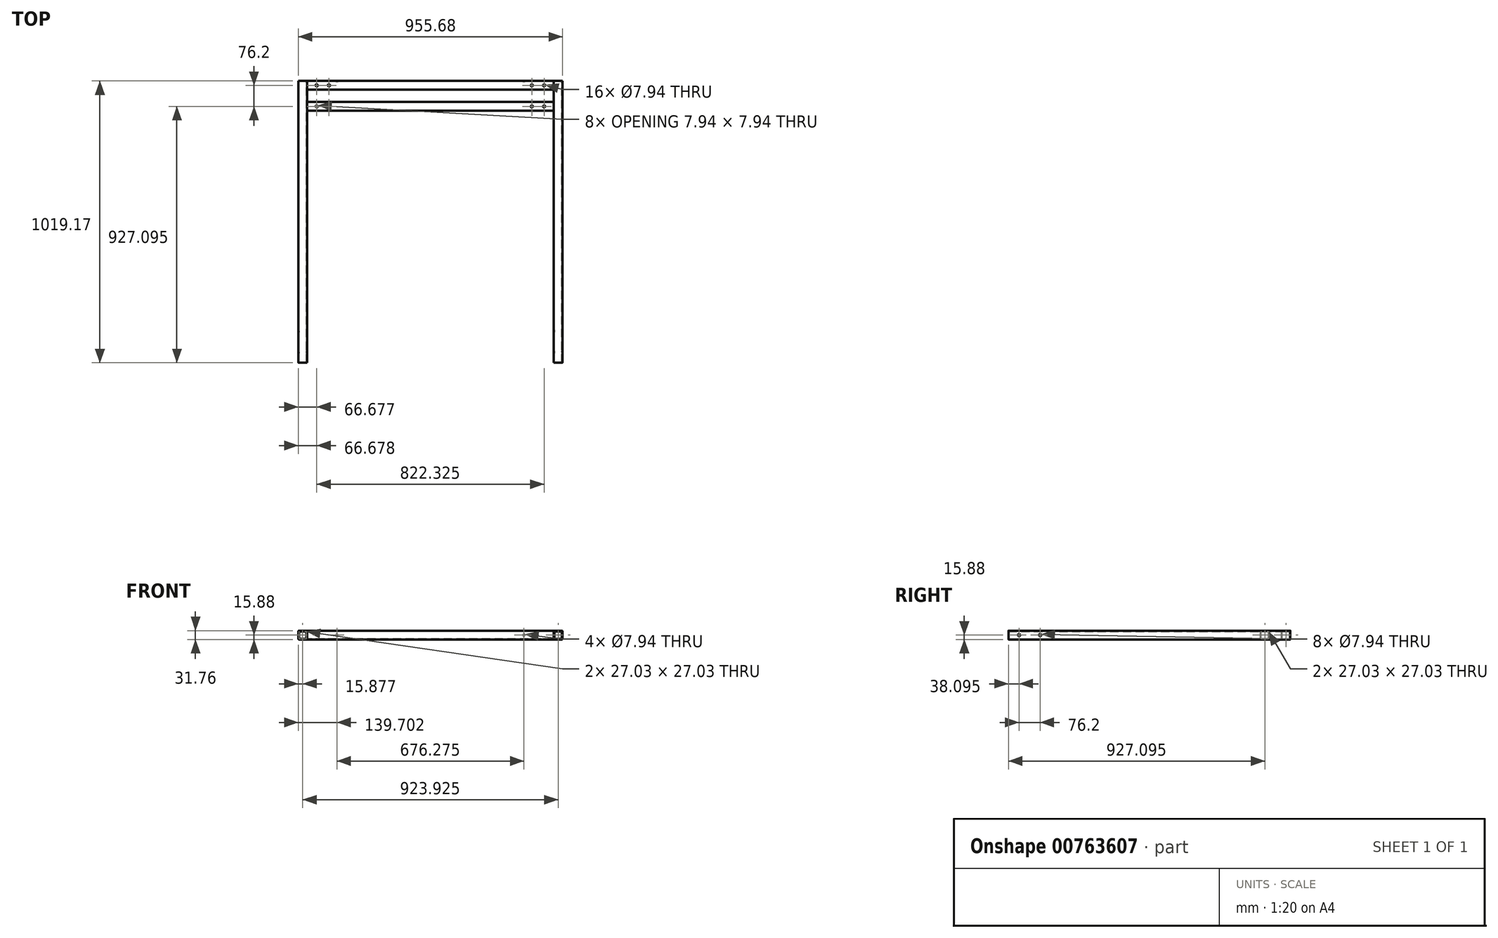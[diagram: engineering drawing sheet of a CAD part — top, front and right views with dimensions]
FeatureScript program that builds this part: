
annotation { "Feature Type Name" : "Feature", "Feature Type Description" : "" }
export const myFeature = defineFeature(function(context is Context, id is Id, definition is map)
    precondition{}
    {
        {
            var Q0;
            Q0=qCreatedBy(makeId("Front.planeOp"),FACE);
            var sketch = newSketch(context, id + "F0", { "sketchPlane" : qUnion([Q0])});
            skLineSegment(sketch, "E0.bottom", {"start": v(-448.45, -15.87) * mm, "end": v(-475.48, -15.87) * mm});
            skLineSegment(sketch, "E0.top", {"start": v(-448.45, 15.88) * mm, "end": v(-475.48, 15.88) * mm});
            skLineSegment(sketch, "E0.left", {"start": v(-446.09, -13.51) * mm, "end": v(-446.09, 13.51) * mm});
            skLineSegment(sketch, "E0.right", {"start": v(-477.84, -13.51) * mm, "end": v(-477.84, 13.51) * mm});
            skPoint(sketch, "E0.middle", {"position": v(-461.96, 0) * mm});
            skPoint(sketch, "E1.visualSharp", {"position": v(-446.09, 15.88) * mm});
            skArc(sketch, "E1.filletArc", {"start": v(-446.09, 13.51) * mm, "mid": v(-446.78, 15.18) * mm, "end": v(-448.45, 15.88) * mm});
            skPoint(sketch, "E2.visualSharp", {"position": v(-446.09, -15.87) * mm});
            skArc(sketch, "E2.filletArc", {"start": v(-448.45, -15.87) * mm, "mid": v(-446.78, -15.18) * mm, "end": v(-446.09, -13.51) * mm});
            skPoint(sketch, "E3.visualSharp", {"position": v(-477.84, -15.87) * mm});
            skArc(sketch, "E3.filletArc", {"start": v(-477.84, -13.51) * mm, "mid": v(-477.15, -15.18) * mm, "end": v(-475.48, -15.87) * mm});
            skPoint(sketch, "E4.visualSharp", {"position": v(-477.84, 15.88) * mm});
            skArc(sketch, "E4.filletArc", {"start": v(-475.48, 15.88) * mm, "mid": v(-477.15, 15.18) * mm, "end": v(-477.84, 13.51) * mm});
            skLineSegment(sketch, "E5.0", {"start": v(-448.45, 13.51) * mm, "end": v(-475.48, 13.51) * mm});
            skLineSegment(sketch, "E5.1", {"start": v(-448.45, -13.51) * mm, "end": v(-448.45, 13.51) * mm});
            skLineSegment(sketch, "E5.2", {"start": v(-448.45, -13.51) * mm, "end": v(-475.48, -13.51) * mm});
            skLineSegment(sketch, "E5.3", {"start": v(-475.48, -13.51) * mm, "end": v(-475.48, 13.51) * mm});
            skLineSegment(sketch, "E6", {"start": v(-461.96, 0) * mm, "end": v(0, 0) * mm, "construction": true});
            skSolve(sketch);
        }
        {
            var Q0;
            Q0=makeQuery(id+"F0.imprint","IMPRINT",FACE,{"disambiguationData":[TD([[makeQuery(id+"F0.imprint","IMPRINT",EDGE,{"derivedFrom":sQuery(id+"F0.wireOp",EDGE,"E0.bottom")}),-1.0]])]});
            extrude(context, id + "F1", {"entities" : qUnion([Q0]), "depth" : 1019.17 * mm, "offsetDistance" : 25.4 * mm});
        }
        {
            var Q0;
            Q0=makeQuery(id+"F1.opExtrude","SWEPT_FACE",FACE,{"disambiguationData":[OSD([sQuery(id+"F0.wireOp",EDGE,"E0.left")])]});
            var sketch = newSketch(context, id + "F2", { "sketchPlane" : qUnion([Q0])});
            skLineSegment(sketch, "E7.bottom", {"start": v(-2.36, -15.88) * mm, "end": v(-29.39, -15.88) * mm});
            skLineSegment(sketch, "E7.top", {"start": v(-2.36, 15.87) * mm, "end": v(-29.39, 15.87) * mm});
            skLineSegment(sketch, "E7.left", {"start": v(0, -13.51) * mm, "end": v(0, 13.51) * mm});
            skLineSegment(sketch, "E7.right", {"start": v(-31.75, -13.51) * mm, "end": v(-31.75, 13.51) * mm});
            skPoint(sketch, "E7.middle", {"position": v(-15.88, 0) * mm});
            skPoint(sketch, "E8.visualSharp", {"position": v(0, 15.87) * mm});
            skArc(sketch, "E8.filletArc", {"start": v(0, 13.51) * mm, "mid": v(-0.7, 15.18) * mm, "end": v(-2.36, 15.87) * mm});
            skPoint(sketch, "E9.visualSharp", {"position": v(0, -15.88) * mm});
            skArc(sketch, "E9.filletArc", {"start": v(-2.36, -15.88) * mm, "mid": v(-0.7, -15.18) * mm, "end": v(0, -13.51) * mm});
            skPoint(sketch, "E10.visualSharp", {"position": v(-31.75, -15.88) * mm});
            skArc(sketch, "E10.filletArc", {"start": v(-31.75, -13.51) * mm, "mid": v(-31.06, -15.18) * mm, "end": v(-29.39, -15.88) * mm});
            skPoint(sketch, "E11.visualSharp", {"position": v(-31.75, 15.87) * mm});
            skArc(sketch, "E11.filletArc", {"start": v(-29.39, 15.87) * mm, "mid": v(-31.06, 15.18) * mm, "end": v(-31.75, 13.51) * mm});
            skLineSegment(sketch, "E12.0", {"start": v(-2.36, 13.51) * mm, "end": v(-29.39, 13.51) * mm});
            skLineSegment(sketch, "E12.1", {"start": v(-2.36, -13.51) * mm, "end": v(-2.36, 13.51) * mm});
            skLineSegment(sketch, "E12.2", {"start": v(-2.36, -13.51) * mm, "end": v(-29.39, -13.51) * mm});
            skLineSegment(sketch, "E12.3", {"start": v(-29.39, -13.51) * mm, "end": v(-29.39, 13.51) * mm});
            skLineSegment(sketch, "E13.bottom", {"start": v(-78.56, -15.88) * mm, "end": v(-105.59, -15.88) * mm});
            skLineSegment(sketch, "E13.top", {"start": v(-78.56, 15.87) * mm, "end": v(-105.59, 15.87) * mm});
            skLineSegment(sketch, "E13.left", {"start": v(-76.2, -13.51) * mm, "end": v(-76.2, 13.51) * mm});
            skLineSegment(sketch, "E13.right", {"start": v(-107.95, -13.51) * mm, "end": v(-107.95, 13.51) * mm});
            skPoint(sketch, "E13.middle", {"position": v(-92.08, 0) * mm});
            skPoint(sketch, "E14.visualSharp", {"position": v(-76.2, 15.87) * mm});
            skArc(sketch, "E14.filletArc", {"start": v(-76.2, 13.51) * mm, "mid": v(-76.9, 15.18) * mm, "end": v(-78.56, 15.87) * mm});
            skPoint(sketch, "E15.visualSharp", {"position": v(-76.2, -15.88) * mm});
            skArc(sketch, "E15.filletArc", {"start": v(-78.56, -15.88) * mm, "mid": v(-76.9, -15.18) * mm, "end": v(-76.2, -13.51) * mm});
            skPoint(sketch, "E16.visualSharp", {"position": v(-107.95, -15.88) * mm});
            skArc(sketch, "E16.filletArc", {"start": v(-107.95, -13.51) * mm, "mid": v(-107.26, -15.18) * mm, "end": v(-105.59, -15.88) * mm});
            skPoint(sketch, "E17.visualSharp", {"position": v(-107.95, 15.87) * mm});
            skArc(sketch, "E17.filletArc", {"start": v(-105.59, 15.87) * mm, "mid": v(-107.26, 15.18) * mm, "end": v(-107.95, 13.51) * mm});
            skLineSegment(sketch, "E18.0", {"start": v(-78.56, 13.51) * mm, "end": v(-105.59, 13.51) * mm});
            skLineSegment(sketch, "E18.1", {"start": v(-78.56, -13.51) * mm, "end": v(-78.56, 13.51) * mm});
            skLineSegment(sketch, "E18.2", {"start": v(-78.56, -13.51) * mm, "end": v(-105.59, -13.51) * mm});
            skLineSegment(sketch, "E18.3", {"start": v(-105.59, -13.51) * mm, "end": v(-105.59, 13.51) * mm});
            skSolve(sketch);
        }
        {
            var Q0;
            {var subQ0=sQuery(id+"F2.wireOp",EDGE,"E13.right");Q0=makeQuery(id+"F2.imprint","IMPRINT",FACE,{"disambiguationData":[TD([[makeQuery(id+"F2.imprint","IMPRINT",EDGE,{"derivedFrom":subQ0}),-1.0]])]});}
            var Q1;
            Q1=makeQuery(id+"F2.imprint","IMPRINT",FACE,{"disambiguationData":[TD([[makeQuery(id+"F2.imprint","IMPRINT",EDGE,{"derivedFrom":sQuery(id+"F2.wireOp",EDGE,"E13.top")}),1.0]])]});
            var Q2;
            {var subQ0=sQuery(id+"F2.wireOp",EDGE,"E13.left");Q2=makeQuery(id+"F2.imprint","IMPRINT",FACE,{"disambiguationData":[TD([[makeQuery(id+"F2.imprint","IMPRINT",EDGE,{"derivedFrom":subQ0}),1.0]])]});}
            var Q3;
            Q3=makeQuery(id+"F2.imprint","IMPRINT",FACE,{"disambiguationData":[TD([[makeQuery(id+"F2.imprint","IMPRINT",EDGE,{"derivedFrom":sQuery(id+"F2.wireOp",EDGE,"E13.bottom")}),-1.0]])]});
            var Q4;
            {var subQ0=sQuery(id+"F2.wireOp",EDGE,"E7.right");Q4=makeQuery(id+"F2.imprint","IMPRINT",FACE,{"disambiguationData":[TD([[makeQuery(id+"F2.imprint","IMPRINT",EDGE,{"derivedFrom":subQ0}),-1.0]])]});}
            var Q5;
            Q5=makeQuery(id+"F2.imprint","IMPRINT",FACE,{"disambiguationData":[TD([[makeQuery(id+"F2.imprint","IMPRINT",EDGE,{"derivedFrom":sQuery(id+"F2.wireOp",EDGE,"E7.top")}),1.0]])]});
            var Q6;
            {var subQ0=sQuery(id+"F2.wireOp",EDGE,"E7.left");Q6=makeQuery(id+"F2.imprint","IMPRINT",FACE,{"disambiguationData":[TD([[makeQuery(id+"F2.imprint","IMPRINT",EDGE,{"derivedFrom":subQ0}),1.0]])]});}
            var Q7;
            Q7=makeQuery(id+"F2.imprint","IMPRINT",FACE,{"disambiguationData":[TD([[makeQuery(id+"F2.imprint","IMPRINT",EDGE,{"derivedFrom":sQuery(id+"F2.wireOp",EDGE,"E7.bottom")}),-1.0]])]});
            extrude(context, id + "F3", {"entities" : qUnion([Q0, Q1, Q2, Q3, Q4, Q5, Q6, Q7]), "depth" : 892.17 * mm, "offsetDistance" : 25.4 * mm});
        }
        {
            var Q0;
            Q0=makeQuery(id+"F1.opExtrude","SWEPT_FACE",FACE,{"disambiguationData":[OSD([sQuery(id+"F0.wireOp",EDGE,"E0.right")])]});
            var sketch = newSketch(context, id + "F4", { "sketchPlane" : qUnion([Q0])});
            skLineSegment(sketch, "E19", {"start": v(1019.18, 0) * mm, "end": v(981.08, 0) * mm, "construction": true});
            skLineSegment(sketch, "E20", {"start": v(981.08, 0) * mm, "end": v(904.88, 0) * mm, "construction": true});
            skSolve(sketch);
        }
        {
            var Q0;
            Q0=sQuery(id+"F4.wireOp",VERTEX,"E19.end");
            var Q1;
            Q1=sQuery(id+"F4.wireOp",VERTEX,"E20.end");
            var Q2;
            Q2=makeQuery(id+"F1.opExtrude","SWEPT_BODY",BODY,{"disambiguationData":[OSD([sQuery(id+"F0.wireOp",EDGE,"E0.bottom"),sQuery(id+"F0.wireOp",EDGE,"E0.top"),sQuery(id+"F0.wireOp",EDGE,"E0.left"),sQuery(id+"F0.wireOp",EDGE,"E0.right"),sQuery(id+"F0.wireOp",EDGE,"E1.filletArc"),sQuery(id+"F0.wireOp",EDGE,"E2.filletArc"),sQuery(id+"F0.wireOp",EDGE,"E3.filletArc"),sQuery(id+"F0.wireOp",EDGE,"E4.filletArc"),sQuery(id+"F0.wireOp",EDGE,"E5.0"),sQuery(id+"F0.wireOp",EDGE,"E5.1"),sQuery(id+"F0.wireOp",EDGE,"E5.2"),sQuery(id+"F0.wireOp",EDGE,"E5.3")])]});
            hole(context, id + "F5", {"style" : HoleStyle.SIMPLE, "endStyle" : HoleEndStyle.THROUGH, "holeDiameter" : 7.94 * mm, "majorDiameter" : 6.35 * mm, "isTappedThrough" : true, "tappedDepth" : 12.7 * mm, "tapClearance" : 3, "locations" : qUnion([Q0, Q1]), "scope" : qUnion([Q2]), "startStyle" : HoleStartStyle.PART});
        }
        {
            var Q0;
            Q0=makeQuery(id+"F1.opExtrude","SWEPT_BODY",BODY,{"disambiguationData":[OSD([sQuery(id+"F0.wireOp",EDGE,"E0.bottom"),sQuery(id+"F0.wireOp",EDGE,"E0.top"),sQuery(id+"F0.wireOp",EDGE,"E0.left"),sQuery(id+"F0.wireOp",EDGE,"E0.right"),sQuery(id+"F0.wireOp",EDGE,"E1.filletArc"),sQuery(id+"F0.wireOp",EDGE,"E2.filletArc"),sQuery(id+"F0.wireOp",EDGE,"E3.filletArc"),sQuery(id+"F0.wireOp",EDGE,"E4.filletArc"),sQuery(id+"F0.wireOp",EDGE,"E5.0"),sQuery(id+"F0.wireOp",EDGE,"E5.1"),sQuery(id+"F0.wireOp",EDGE,"E5.2"),sQuery(id+"F0.wireOp",EDGE,"E5.3")])]});
            var Q1;
            Q1=qCreatedBy(makeId("Right.planeOp"),FACE);
            mirror(context, id + "F6", {"entities" : qUnion([Q0]), "mirrorPlane" : qUnion([Q1])});
        }
        {
            var Q0;
            Q0=makeQuery(id+"F3.opExtrude","SWEPT_FACE",FACE,{"disambiguationData":[OSD([sQuery(id+"F2.wireOp",EDGE,"E7.left")])]});
            var sketch = newSketch(context, id + "F7", { "sketchPlane" : qUnion([Q0])});
            skLineSegment(sketch, "E21", {"start": v(477.84, 0) * mm, "end": v(338.14, 0) * mm, "construction": true});
            skSolve(sketch);
        }
        {
            var Q0;
            Q0=sQuery(id+"F7.wireOp",VERTEX,"E21.end");
            var Q1;
            Q1=makeQuery(id+"F3.opExtrude","SWEPT_BODY",BODY,{"disambiguationData":[OSD([sQuery(id+"F2.wireOp",EDGE,"E7.bottom"),sQuery(id+"F2.wireOp",EDGE,"E7.top"),sQuery(id+"F2.wireOp",EDGE,"E7.left"),sQuery(id+"F2.wireOp",EDGE,"E7.right"),sQuery(id+"F2.wireOp",EDGE,"E8.filletArc"),sQuery(id+"F2.wireOp",EDGE,"E9.filletArc"),sQuery(id+"F2.wireOp",EDGE,"E10.filletArc"),sQuery(id+"F2.wireOp",EDGE,"E11.filletArc"),sQuery(id+"F2.wireOp",EDGE,"E12.0"),sQuery(id+"F2.wireOp",EDGE,"E12.1"),sQuery(id+"F2.wireOp",EDGE,"E12.2"),sQuery(id+"F2.wireOp",EDGE,"E12.3")])]});
            hole(context, id + "F8", {"style" : HoleStyle.SIMPLE, "endStyle" : HoleEndStyle.THROUGH, "holeDiameter" : 7.94 * mm, "majorDiameter" : 6.35 * mm, "isTappedThrough" : true, "tappedDepth" : 12.7 * mm, "tapClearance" : 3, "locations" : qUnion([Q0]), "scope" : qUnion([Q1]), "startStyle" : HoleStartStyle.PART});
        }
        {
            var Q0;
            Q0=makeQuery(id+"F3.opExtrude","SWEPT_FACE",FACE,{"disambiguationData":[OSD([sQuery(id+"F2.wireOp",EDGE,"E7.left")])]});
            var sketch = newSketch(context, id + "F9", { "sketchPlane" : qUnion([Q0])});
            skLineSegment(sketch, "E22", {"start": v(-477.84, 0) * mm, "end": v(-338.14, 0) * mm, "construction": true});
            skSolve(sketch);
        }
        {
            var Q0;
            Q0=sQuery(id+"F9.wireOp",VERTEX,"E22.end");
            var Q1;
            Q1=makeQuery(id+"F3.opExtrude","SWEPT_BODY",BODY,{"disambiguationData":[OSD([sQuery(id+"F2.wireOp",EDGE,"E7.bottom"),sQuery(id+"F2.wireOp",EDGE,"E7.top"),sQuery(id+"F2.wireOp",EDGE,"E7.left"),sQuery(id+"F2.wireOp",EDGE,"E7.right"),sQuery(id+"F2.wireOp",EDGE,"E8.filletArc"),sQuery(id+"F2.wireOp",EDGE,"E9.filletArc"),sQuery(id+"F2.wireOp",EDGE,"E10.filletArc"),sQuery(id+"F2.wireOp",EDGE,"E11.filletArc"),sQuery(id+"F2.wireOp",EDGE,"E12.0"),sQuery(id+"F2.wireOp",EDGE,"E12.1"),sQuery(id+"F2.wireOp",EDGE,"E12.2"),sQuery(id+"F2.wireOp",EDGE,"E12.3")])]});
            hole(context, id + "F10", {"style" : HoleStyle.SIMPLE, "endStyle" : HoleEndStyle.THROUGH, "holeDiameter" : 7.94 * mm, "majorDiameter" : 6.35 * mm, "isTappedThrough" : true, "tappedDepth" : 12.7 * mm, "tapClearance" : 3, "locations" : qUnion([Q0]), "scope" : qUnion([Q1]), "startStyle" : HoleStartStyle.PART});
        }
        {
            var Q0;
            Q0=makeQuery(id+"F3.opExtrude","SWEPT_FACE",FACE,{"disambiguationData":[OSD([sQuery(id+"F2.wireOp",EDGE,"E13.top")])]});
            var sketch = newSketch(context, id + "F11", { "sketchPlane" : qUnion([Q0])});
            skLineSegment(sketch, "E23", {"start": v(-446.09, -92.08) * mm, "end": v(-411.16, -92.08) * mm, "construction": true});
            skLineSegment(sketch, "E24", {"start": v(-411.16, -92.08) * mm, "end": v(-366.71, -92.08) * mm, "construction": true});
            skLineSegment(sketch, "E25", {"start": v(446.09, -92.08) * mm, "end": v(411.16, -92.08) * mm, "construction": true});
            skLineSegment(sketch, "E26", {"start": v(411.16, -92.08) * mm, "end": v(366.71, -92.08) * mm, "construction": true});
            skSolve(sketch);
        }
        {
            var Q0;
            Q0=sQuery(id+"F11.wireOp",VERTEX,"E25.end");
            var Q1;
            Q1=sQuery(id+"F11.wireOp",VERTEX,"E26.end");
            var Q2;
            Q2=sQuery(id+"F11.wireOp",VERTEX,"E24.end");
            var Q3;
            Q3=sQuery(id+"F11.wireOp",VERTEX,"E23.end");
            var Q4;
            Q4=makeQuery(id+"F3.opExtrude","SWEPT_BODY",BODY,{"disambiguationData":[OSD([sQuery(id+"F2.wireOp",EDGE,"E13.bottom"),sQuery(id+"F2.wireOp",EDGE,"E13.top"),sQuery(id+"F2.wireOp",EDGE,"E13.left"),sQuery(id+"F2.wireOp",EDGE,"E13.right"),sQuery(id+"F2.wireOp",EDGE,"E14.filletArc"),sQuery(id+"F2.wireOp",EDGE,"E15.filletArc"),sQuery(id+"F2.wireOp",EDGE,"E16.filletArc"),sQuery(id+"F2.wireOp",EDGE,"E17.filletArc"),sQuery(id+"F2.wireOp",EDGE,"E18.0"),sQuery(id+"F2.wireOp",EDGE,"E18.1"),sQuery(id+"F2.wireOp",EDGE,"E18.2"),sQuery(id+"F2.wireOp",EDGE,"E18.3")])]});
            hole(context, id + "F12", {"style" : HoleStyle.SIMPLE, "endStyle" : HoleEndStyle.THROUGH, "holeDiameter" : 7.94 * mm, "majorDiameter" : 6.35 * mm, "isTappedThrough" : true, "tappedDepth" : 12.7 * mm, "tapClearance" : 3, "locations" : qUnion([Q0, Q1, Q2, Q3]), "scope" : qUnion([Q4]), "startStyle" : HoleStartStyle.PART});
        }
        {
            var Q0;
            Q0=makeQuery(id+"F3.opExtrude","SWEPT_FACE",FACE,{"disambiguationData":[OSD([sQuery(id+"F2.wireOp",EDGE,"E7.top")])]});
            var sketch = newSketch(context, id + "F13", { "sketchPlane" : qUnion([Q0])});
            skLineSegment(sketch, "E27", {"start": v(446.09, -15.88) * mm, "end": v(411.16, -15.88) * mm, "construction": true});
            skLineSegment(sketch, "E28", {"start": v(411.16, -15.88) * mm, "end": v(366.71, -15.88) * mm, "construction": true});
            skLineSegment(sketch, "E29", {"start": v(-446.09, -15.88) * mm, "end": v(-411.16, -15.88) * mm, "construction": true});
            skLineSegment(sketch, "E30", {"start": v(-411.16, -15.88) * mm, "end": v(-366.71, -15.88) * mm, "construction": true});
            skSolve(sketch);
        }
        {
            var Q0;
            Q0=sQuery(id+"F13.wireOp",VERTEX,"E27.end");
            var Q1;
            Q1=sQuery(id+"F13.wireOp",VERTEX,"E28.end");
            var Q2;
            Q2=sQuery(id+"F13.wireOp",VERTEX,"E30.end");
            var Q3;
            Q3=sQuery(id+"F13.wireOp",VERTEX,"E29.end");
            var Q4;
            Q4=makeQuery(id+"F3.opExtrude","SWEPT_BODY",BODY,{"disambiguationData":[OSD([sQuery(id+"F2.wireOp",EDGE,"E7.bottom"),sQuery(id+"F2.wireOp",EDGE,"E7.top"),sQuery(id+"F2.wireOp",EDGE,"E7.left"),sQuery(id+"F2.wireOp",EDGE,"E7.right"),sQuery(id+"F2.wireOp",EDGE,"E8.filletArc"),sQuery(id+"F2.wireOp",EDGE,"E9.filletArc"),sQuery(id+"F2.wireOp",EDGE,"E10.filletArc"),sQuery(id+"F2.wireOp",EDGE,"E11.filletArc"),sQuery(id+"F2.wireOp",EDGE,"E12.0"),sQuery(id+"F2.wireOp",EDGE,"E12.1"),sQuery(id+"F2.wireOp",EDGE,"E12.2"),sQuery(id+"F2.wireOp",EDGE,"E12.3")])]});
            hole(context, id + "F14", {"style" : HoleStyle.SIMPLE, "endStyle" : HoleEndStyle.THROUGH, "holeDiameter" : 7.94 * mm, "majorDiameter" : 6.35 * mm, "isTappedThrough" : true, "tappedDepth" : 12.7 * mm, "tapClearance" : 3, "locations" : qUnion([Q0, Q1, Q2, Q3]), "scope" : qUnion([Q4]), "startStyle" : HoleStartStyle.PART});
        }
    });
